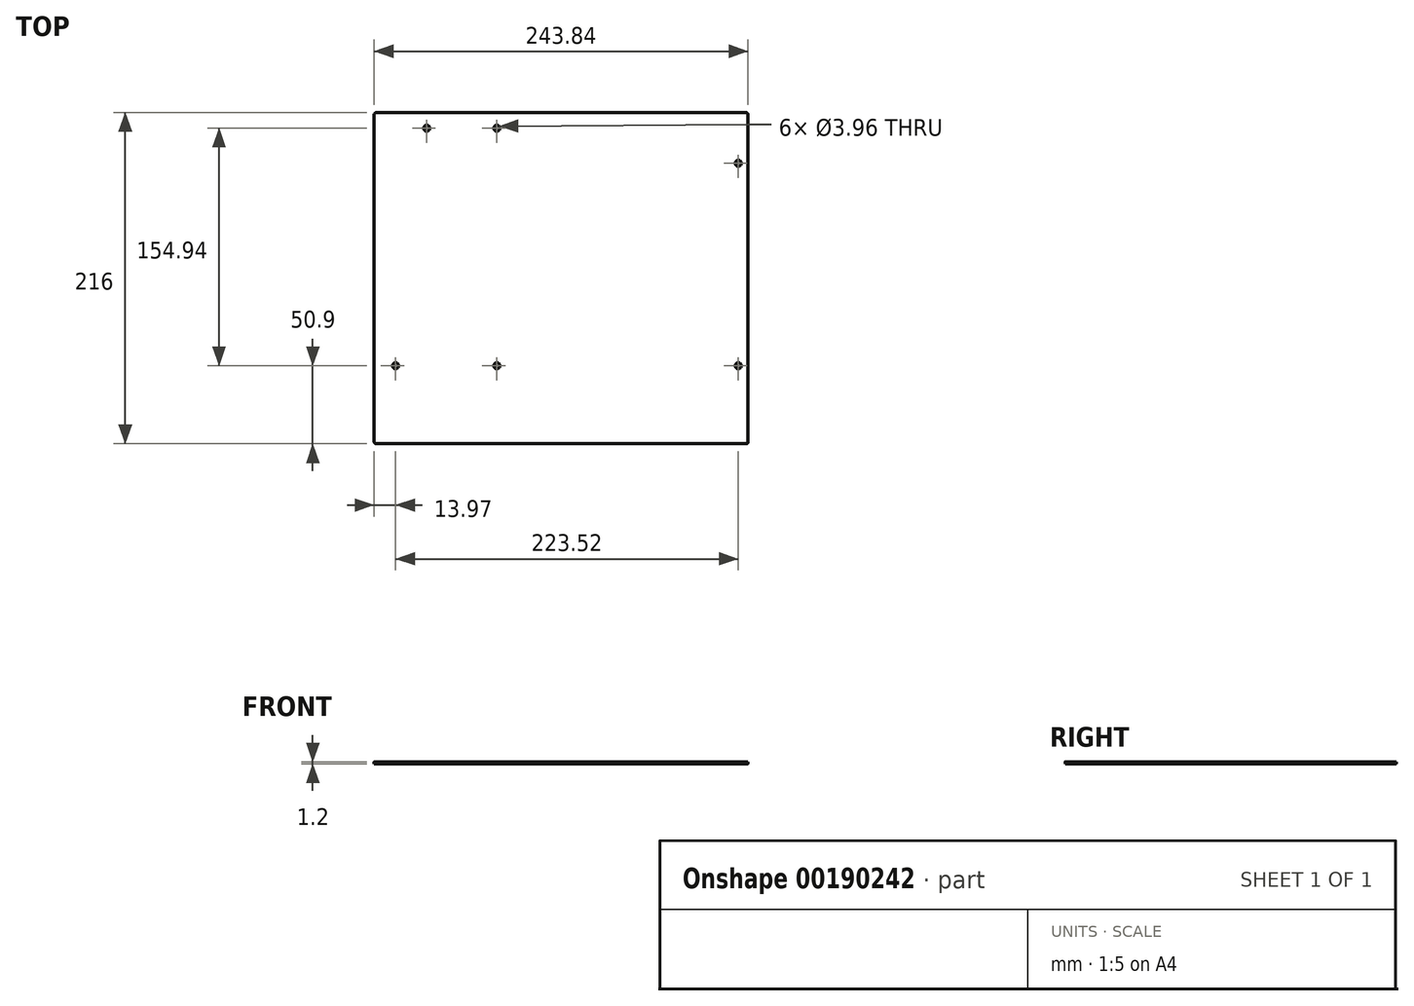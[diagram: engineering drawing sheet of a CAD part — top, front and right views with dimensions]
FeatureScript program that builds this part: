
annotation { "Feature Type Name" : "Feature", "Feature Type Description" : "" }
export const myFeature = defineFeature(function(context is Context, id is Id, definition is map)
    precondition{}
    {
        {
            var Q0;
            Q0=qCreatedBy(makeId("Top.planeOp"),FACE);
            var sketch = newSketch(context, id + "F0", { "sketchPlane" : qUnion([Q0])});
            skLineSegment(sketch, "E0.bottom", {"start": v(-121.92, 108) * mm, "end": v(121.92, 108) * mm});
            skLineSegment(sketch, "E0.top", {"start": v(-121.92, -108) * mm, "end": v(121.92, -108) * mm});
            skLineSegment(sketch, "E0.left", {"start": v(-121.92, 108) * mm, "end": v(-121.92, -108) * mm});
            skLineSegment(sketch, "E0.right", {"start": v(121.92, 108) * mm, "end": v(121.92, -108) * mm});
            skLineSegment(sketch, "E1", {"start": v(-87.63, 108) * mm, "end": v(-87.63, -108) * mm, "construction": true});
            skLineSegment(sketch, "E2", {"start": v(-107.95, -108) * mm, "end": v(-107.95, 108) * mm, "construction": true});
            skLineSegment(sketch, "E3", {"start": v(-121.92, -57.1) * mm, "end": v(121.92, -57.1) * mm, "construction": true});
            skLineSegment(sketch, "E4", {"start": v(-121.92, 97.84) * mm, "end": v(121.92, 97.84) * mm, "construction": true});
            skLineSegment(sketch, "E5", {"start": v(-41.91, 108) * mm, "end": v(-41.91, -108) * mm, "construction": true});
            skLineSegment(sketch, "E6", {"start": v(121.92, 74.98) * mm, "end": v(-121.92, 74.98) * mm, "construction": true});
            skPoint(sketch, "E7", {"position": v(0, 108) * mm});
            skPoint(sketch, "E8", {"position": v(121.92, 0) * mm});
            skCircle(sketch, "E9", {"center": v(-87.63, 97.84) * mm, "radius": 1.98 * mm});
            skCircle(sketch, "E10", {"center": v(-41.91, 97.84) * mm, "radius": 1.98 * mm});
            skCircle(sketch, "E11", {"center": v(-41.91, -57.1) * mm, "radius": 1.98 * mm});
            skCircle(sketch, "E12", {"center": v(-107.95, -57.1) * mm, "radius": 1.98 * mm});
            skLineSegment(sketch, "E13", {"start": v(115.57, 108) * mm, "end": v(115.57, -108) * mm, "construction": true});
            skCircle(sketch, "E14", {"center": v(115.57, 74.98) * mm, "radius": 1.98 * mm});
            skCircle(sketch, "E15", {"center": v(115.57, -57.1) * mm, "radius": 1.98 * mm});
            skSolve(sketch);
        }
        {
            var Q0;
            Q0=makeQuery(id+"F0.imprint","IMPRINT",FACE,{"disambiguationData":[TD([[makeQuery(id+"F0.imprint","IMPRINT",EDGE,{"derivedFrom":sQuery(id+"F0.wireOp",EDGE,"E0.bottom")}),-1.0]])]});
            extrude(context, id + "F1", {"entities" : qUnion([Q0]), "depth" : 1.2 * mm});
        }
        {
            var Q0;
            Q0=makeQuery(id+"F1.opExtrude","SWEPT_EDGE",EDGE,{"disambiguationData":[OSD([sQuery(id+"F0.wireOp",EDGE,"E0.top"),sQuery(id+"F0.wireOp",EDGE,"E0.left")])]});
            var Q1;
            Q1=makeQuery(id+"F1.opExtrude","SWEPT_EDGE",EDGE,{"disambiguationData":[OSD([sQuery(id+"F0.wireOp",EDGE,"E0.top"),sQuery(id+"F0.wireOp",EDGE,"E0.right")])]});
            var Q2;
            Q2=makeQuery(id+"F1.opExtrude","SWEPT_EDGE",EDGE,{"disambiguationData":[OSD([sQuery(id+"F0.wireOp",EDGE,"E0.bottom"),sQuery(id+"F0.wireOp",EDGE,"E0.left")])]});
            var Q3;
            Q3=makeQuery(id+"F1.opExtrude","SWEPT_EDGE",EDGE,{"disambiguationData":[OSD([sQuery(id+"F0.wireOp",EDGE,"E0.bottom"),sQuery(id+"F0.wireOp",EDGE,"E0.right")])]});
            fillet(context, id + "F2", {"entities" : qUnion([Q0, Q1, Q2, Q3]), "radius" : 1.3 * mm, "tangentPropagation" : true, "allowEdgeOverflow" : false});
        }
    });
